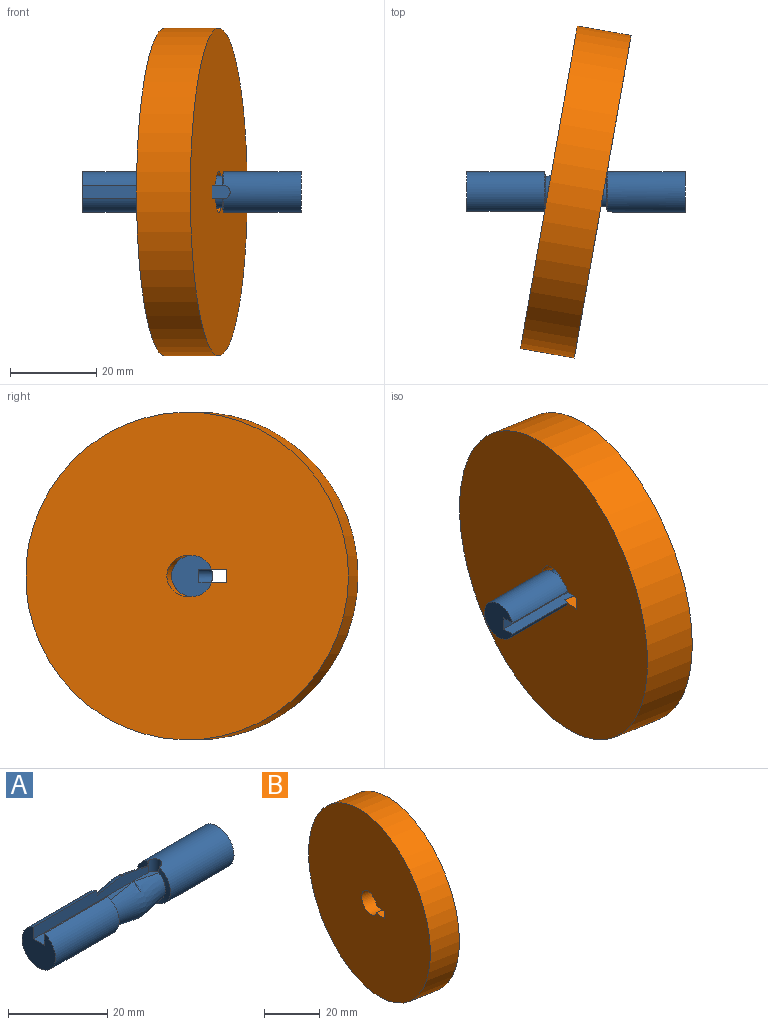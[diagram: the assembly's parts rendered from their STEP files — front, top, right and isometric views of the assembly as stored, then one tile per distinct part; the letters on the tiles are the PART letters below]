
ASSEMBLY  parts=2 mates=1
PART A: 11 faces, bbox 50.9x9.6x9.6 mm
  f0: cone r=3.59mm half-angle=80deg, axis (1,0,0), area 27.4mm2, adj f1,f5,f7,f8
  f1: revolved ~14.16x9.52mm, area 332.6mm2, adj f0,f2,f7,f8
  f2: cone r=4.76mm half-angle=80deg, axis (-1,0,0), area 27.4mm2, adj f1,f3,f7,f8
  f3: cylinder r=4.76mm len=18.11mm, axis (-1,0,0), area 483.4mm2, adj f2,f4,f7,f8
  f4: plane 9.53x9.25mm, normal (-1,0,0), area 61.5mm2, adj f3,f7,f8,f10
  f5: cylinder r=4.76mm len=18.11mm, axis (-1,0,0), area 538mm2, adj f0,f6,f9
  f6: plane 9.53x9.53mm, normal (1,0,0), area 71.3mm2, adj f5
  f7: plane 32.76x2.97mm, normal (0,-1,0), area 86.1mm2, adj f0,f1,f2,f3,f4,f9,f10
  f8: plane 32.76x2.97mm, normal (0,1,0), area 86.1mm2, adj f0,f1,f2,f3,f4,f9,f10
  f9: cylinder r=1.59mm len=3.18mm, axis (0,0,1), area 14.5mm2, adj f5,f7,f8,f10
  f10: plane 34.28x3.18mm, normal (0,0,1), area 107.7mm2, adj f4,f7,f8,f9
PART B: 7 faces, bbox 25.7x77.2x76.2 mm
  f0: cylinder r=4.76mm len=14.11mm, axis (-0.98,0.17,0), area 338.9mm2, adj f1,f2,f4,f5
  f1: plane 76.2x75.04mm, normal (-0.98,0.17,0), area 4474.8mm2, adj f0,f3,f4,f5,f6
  f2: plane 76.2x75.04mm, normal (0.98,-0.17,0), area 4474.8mm2, adj f0,f3,f4,f5,f6
  f3: cylinder r=38.1mm len=77.25mm, axis (-0.98,0.17,0), area 3040.2mm2, adj f1,f2
  f4: plane 13.32x6.83mm, normal (0,0,1), area 59.6mm2, adj f0,f1,f2,f6
  f5: plane 13.32x6.83mm, normal (0,0,-1), area 59.6mm2, adj f0,f1,f2,f6
  f6: plane 12.51x3.18mm, normal (0.17,0.98,0), area 40.3mm2, adj f1,f2,f4,f5
PLACE A rot(axis=(1,0,0),90deg) t=(-20.56,10.42,-12.13)mm
PLACE B t=(-20.6,10.47,-12.13)mm
MATE planar A.f8 <-> B.f4  axis (0,0,1) through (-5.14,7.48,-13.71)mm
